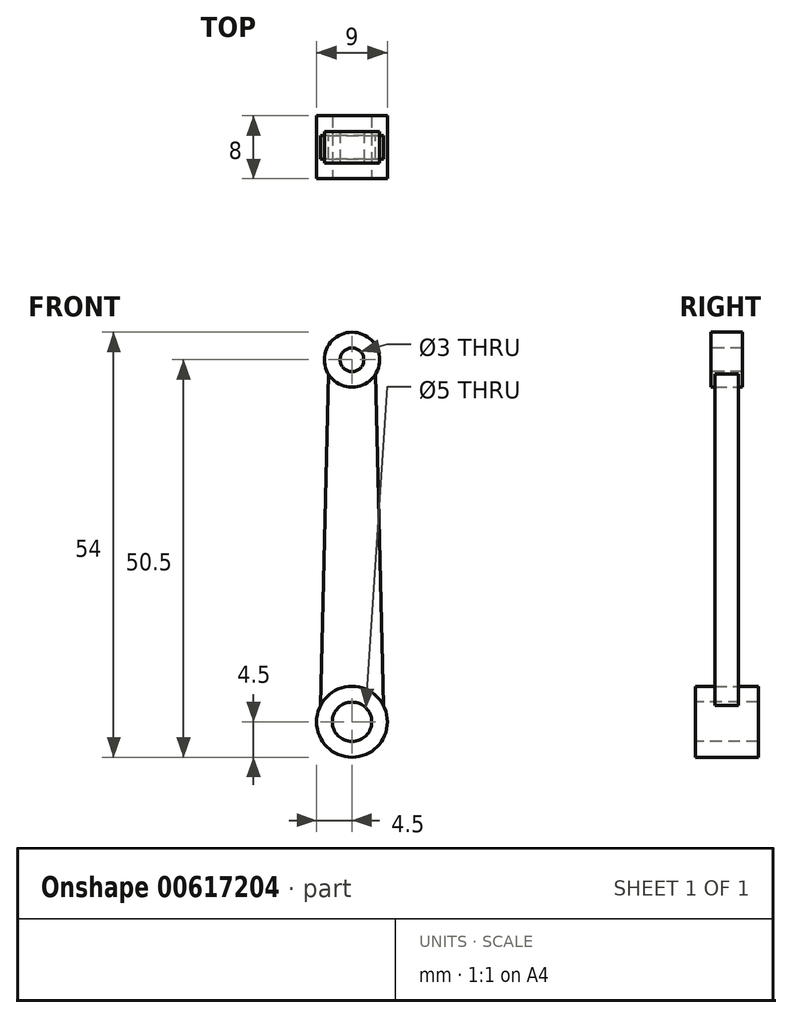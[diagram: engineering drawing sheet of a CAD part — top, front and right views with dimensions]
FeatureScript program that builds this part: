
annotation { "Feature Type Name" : "Feature", "Feature Type Description" : "" }
export const myFeature = defineFeature(function(context is Context, id is Id, definition is map)
    precondition{}
    {
        {
            var Q0;
            Q0=qCreatedBy(makeId("Front.planeOp"),FACE);
            var sketch = newSketch(context, id + "F0", { "sketchPlane" : qUnion([Q0])});
            skCircle(sketch, "E0", {"center": v(0, 0) * mm, "radius": 4.5 * mm});
            skSolve(sketch);
        }
        {
            var Q0;
            Q0 = qSketchRegion(id + "F0", true);
            extrude(context, id + "F1", {"entities" : qUnion([Q0]), "endBound" : BoundingType.SYMMETRIC, "depth" : 8 * mm, "offsetDistance" : 25 * mm});
        }
        {
            var Q0;
            Q0=qCreatedBy(makeId("Front.planeOp"),FACE);
            var sketch = newSketch(context, id + "F2", { "sketchPlane" : qUnion([Q0])});
            skCircle(sketch, "E1", {"center": v(0, 46) * mm, "radius": 3.5 * mm});
            skLineSegment(sketch, "E2", {"start": v(0, 46) * mm, "end": v(0, 0) * mm, "construction": true});
            skSolve(sketch);
        }
        {
            var Q0;
            Q0 = qSketchRegion(id + "F2", true);
            extrude(context, id + "F3", {"entities" : qUnion([Q0]), "endBound" : BoundingType.SYMMETRIC, "depth" : 4 * mm, "offsetDistance" : 25 * mm});
        }
        {
            var Q0;
            Q0=qCreatedBy(makeId("Front.planeOp"),FACE);
            var sketch = newSketch(context, id + "F4", { "sketchPlane" : qUnion([Q0])});
            skLineSegment(sketch, "E3", {"start": v(-3, 44.2) * mm, "end": v(-4, 2.06) * mm});
            skLineSegment(sketch, "E4.MirrorCS", {"start": v(3, 44.2) * mm, "end": v(4, 2.06) * mm});
            skArc(sketch, "E5.0", {"start": v(-3, 44.2) * mm, "mid": v(0, 42.5) * mm, "end": v(3, 44.2) * mm});
            skArc(sketch, "E6.0", {"start": v(4, 2.06) * mm, "mid": v(0, 4.5) * mm, "end": v(-4, 2.06) * mm});
            skSolve(sketch);
        }
        {
            var Q0;
            Q0 = qSketchRegion(id + "F4", true);
            extrude(context, id + "F5", {"entities" : qUnion([Q0]), "endBound" : BoundingType.SYMMETRIC, "depth" : 3 * mm, "offsetDistance" : 25 * mm});
        }
        {
            var Q0;
            Q0=makeQuery(id+"F1.opExtrude","CAP_FACE",FACE,{"disambiguationData":[OSD([sQuery(id+"F0.wireOp",EDGE,"E0")])],"isStart":false});
            var sketch = newSketch(context, id + "F6", { "sketchPlane" : qUnion([Q0])});
            skLineSegment(sketch, "E7", {"start": v(0, 0) * mm, "end": v(0, 46) * mm, "construction": true});
            skSolve(sketch);
        }
        {
            var Q0;
            Q0=sQuery(id+"F6.wireOp",VERTEX,"E7.start");
            var Q1;
            Q1=makeQuery(id+"F1.opExtrude","SWEPT_BODY",BODY,{"disambiguationData":[OSD([sQuery(id+"F0.wireOp",EDGE,"E0")])]});
            hole(context, id + "F7", {"style" : HoleStyle.SIMPLE, "endStyle" : HoleEndStyle.THROUGH, "standardTappedOrClearance" : lookupTablePath({ "standard" : "ISO", "size" : "5", "type" : "Drilled" }), "standardBlindInLast" : lookupTablePath({ "standard" : "ISO", "size" : "5", "type" : "Drilled" }), "holeDiameter" : 5 * mm, "majorDiameter" : 5 * mm, "isTappedThrough" : true, "tappedDepth" : 12 * mm, "tapClearance" : 3, "locations" : qUnion([Q0]), "scope" : qUnion([Q1])});
        }
        {
            var Q0;
            Q0=sQuery(id+"F6.wireOp",VERTEX,"E7.end");
            var Q1;
            Q1=makeQuery(id+"F3.opExtrude","SWEPT_BODY",BODY,{"disambiguationData":[OSD([sQuery(id+"F2.wireOp",EDGE,"E1")])]});
            hole(context, id + "F8", {"style" : HoleStyle.SIMPLE, "endStyle" : HoleEndStyle.THROUGH, "standardTappedOrClearance" : lookupTablePath({ "standard" : "ISO", "size" : "3", "type" : "Drilled" }), "standardBlindInLast" : lookupTablePath({ "standard" : "ISO", "size" : "3", "type" : "Drilled" }), "holeDiameter" : 3 * mm, "majorDiameter" : 5 * mm, "isTappedThrough" : true, "tappedDepth" : 12 * mm, "tapClearance" : 3, "locations" : qUnion([Q0]), "scope" : qUnion([Q1])});
        }
    });
